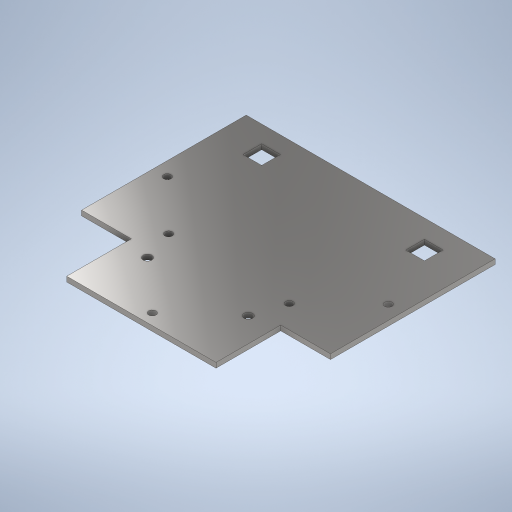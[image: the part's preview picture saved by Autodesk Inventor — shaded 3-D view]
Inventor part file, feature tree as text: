
AUTODESK INVENTOR PART (.ipt)
format: ipt  version: 2023 (Build 270158000, 158)  size: 296,960 bytes
history: native  units: mm
features: reference x13, other x8, extrude x5, sketch x5, projected_geometry x2
ambient origin geometry x8: Origin, YZ Plane, XZ Plane, XY Plane, X Axis, Y Axis, Z Axis, Center Point
bodies: Body1 (feature_tree)
feature tree (33):
  other  "Bryła1"
  extrude  "Wyciągnięcie proste1"  Depth=2.0mm TaperAngle=0.0deg
  extrude  "Wyciągnięcie proste2"  Depth=2.0mm TaperAngle=0.0deg
  extrude  "Wyciągnięcie proste3"  TaperAngle=0.0deg  [1 undecoded]
  extrude  "Wyciągnięcie proste4"  Depth=7.5mm
  extrude  "Wyciągnięcie proste6"  Depth=7.5mm
  sketch  "Szkic1"
  sketch  "Szkic2"
  reference  "Odniesienie1"
  reference  "Odniesienie2"
  reference  "Odniesienie3"
  reference  "Odniesienie4"
  sketch  "Szkic3"
  projected_geometry  "Pętla rzutowana1"
  reference  "Odniesienie5"
  sketch  "Szkic4"
  reference  "Odniesienie6"
  reference  "Odniesienie7"
  reference  "Odniesienie8"
  reference  "Odniesienie9"
  reference  "Odniesienie10"
  reference  "Odniesienie11"
  reference  "Odniesienie12"
  reference  "Odniesienie13"
  sketch  "Szkic6"
  projected_geometry  "Pętla rzutowana3"
  other  "<userpath>\Desktop\MojeRoboty\Stefan\mechanics 2\STEFAN.iam"
  other  "STEFAN.iam"
  other  "sciana_prawa_nowa:1"
  other  "sciana_prawa_nowa_MIR:1"
  other  "plug_2:1"
  other  "plytka_dol:1"
  other  "Board_1:1"
note: 1 required parameter value undecoded (feature->parameter linkage not recoverable at this tier; creation-order binding heuristic only, values carry confidence <= 0.55)
